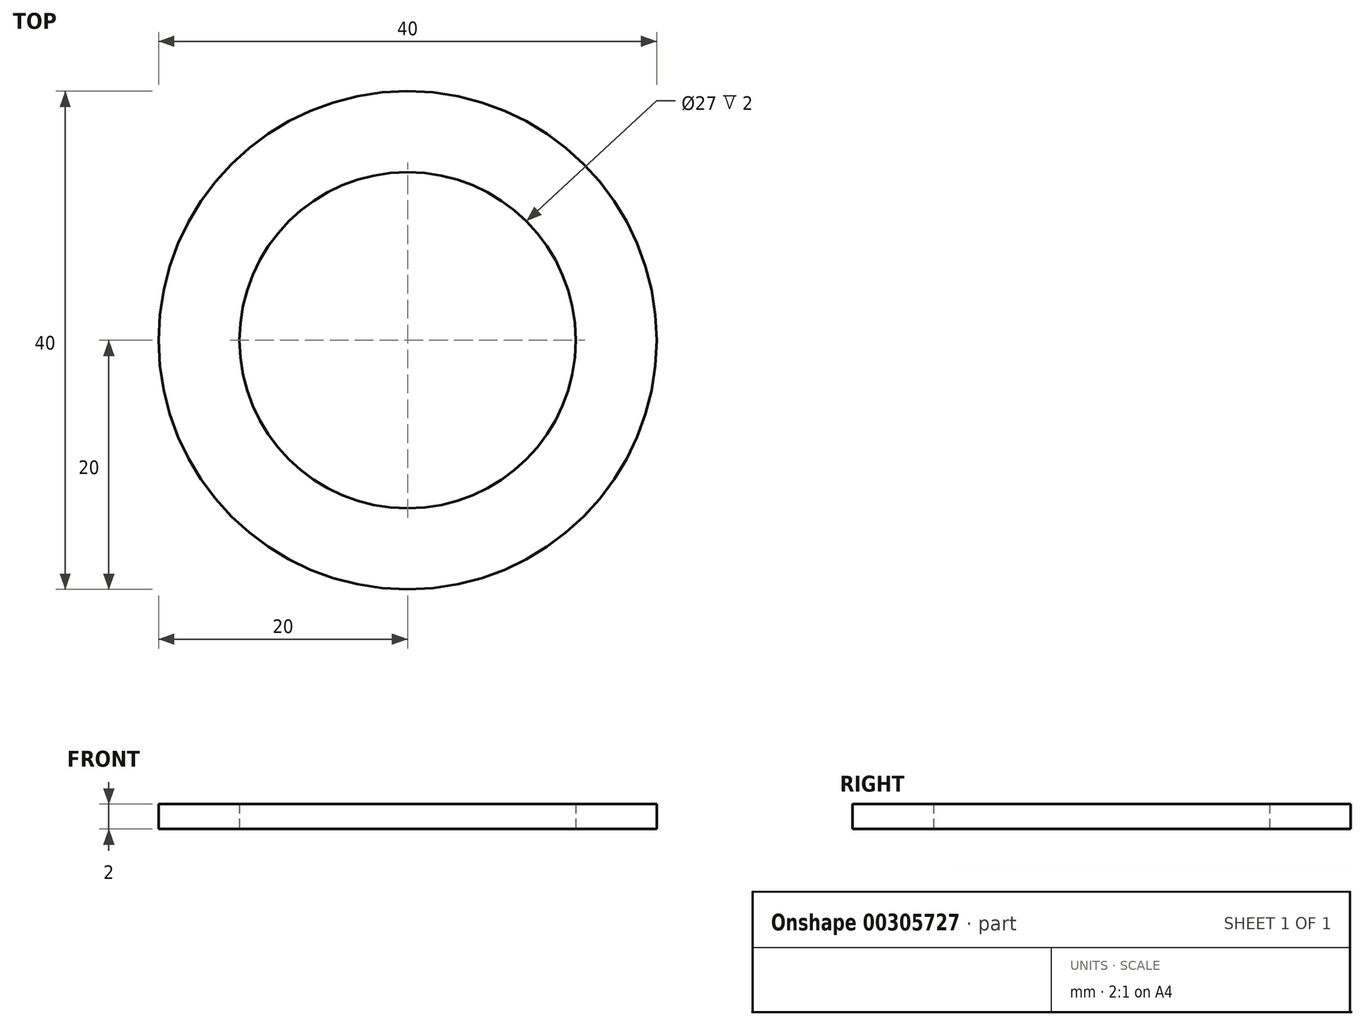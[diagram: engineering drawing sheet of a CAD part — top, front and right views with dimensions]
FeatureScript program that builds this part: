
annotation { "Feature Type Name" : "Feature", "Feature Type Description" : "" }
export const myFeature = defineFeature(function(context is Context, id is Id, definition is map)
    precondition{}
    {
        {
            var Q0;
            Q0=qCreatedBy(makeId("Top.planeOp"),FACE);
            var sketch = newSketch(context, id + "F0", { "sketchPlane" : qUnion([Q0])});
            skCircle(sketch, "E0", {"center": v(0, 0) * mm, "radius": 20 * mm});
            skCircle(sketch, "E1", {"center": v(0, 0) * mm, "radius": 13.5 * mm});
            skSolve(sketch);
        }
        {
            var Q0;
            Q0 = qSketchRegion(id + "F0", true);
            extrude(context, id + "F1", {"entities" : qUnion([Q0]), "depth" : 2 * mm});
        }
    });
